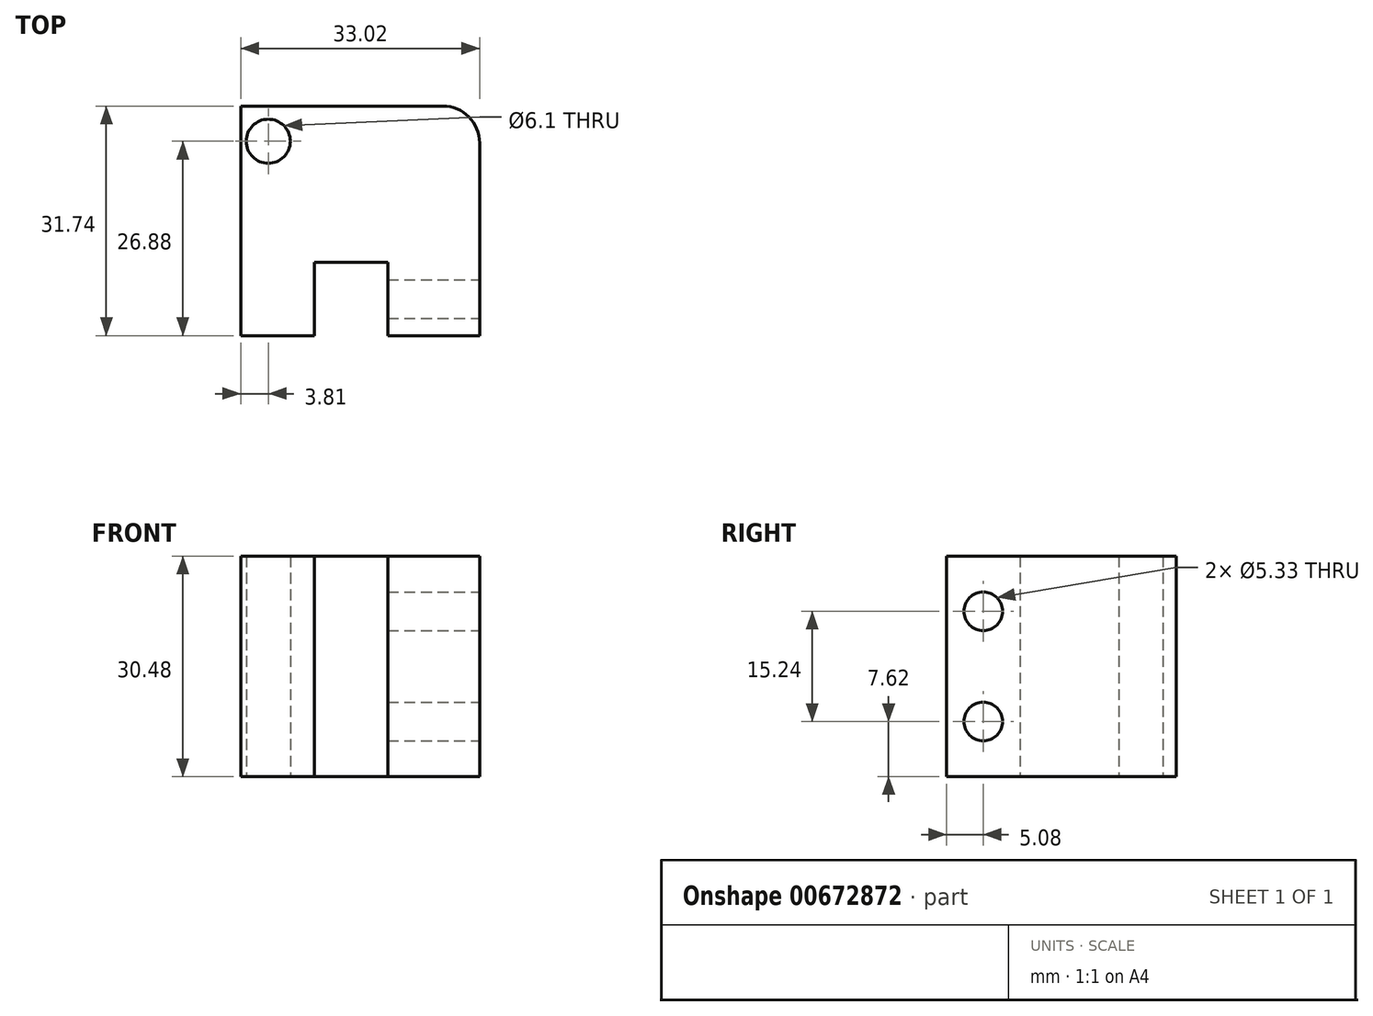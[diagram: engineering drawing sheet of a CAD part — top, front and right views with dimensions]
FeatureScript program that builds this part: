
annotation { "Feature Type Name" : "Feature", "Feature Type Description" : "" }
export const myFeature = defineFeature(function(context is Context, id is Id, definition is map)
    precondition{}
    {
        {
            var Q0;
            Q0=qCreatedBy(makeId("Top.planeOp"),FACE);
            var sketch = newSketch(context, id + "F0", { "sketchPlane" : qUnion([Q0])});
            skLineSegment(sketch, "E0.bottom", {"start": v(-10.16, -6.35) * mm, "end": v(0, -6.35) * mm});
            skLineSegment(sketch, "E0.right", {"start": v(12.7, -6.35) * mm, "end": v(12.7, 15.23) * mm});
            skPoint(sketch, "E0.middle", {"position": v(0, 0) * mm});
            skLineSegment(sketch, "E1", {"start": v(-10.16, -16.51) * mm, "end": v(-10.16, -6.35) * mm});
            skLineSegment(sketch, "E2", {"start": v(12.7, -6.35) * mm, "end": v(12.7, -16.51) * mm});
            skLineSegment(sketch, "E3", {"start": v(12.7, -16.51) * mm, "end": v(0, -16.51) * mm});
            skLineSegment(sketch, "E4", {"start": v(0, -16.51) * mm, "end": v(0, -6.35) * mm});
            skLineSegment(sketch, "E5", {"start": v(-10.16, -16.51) * mm, "end": v(-16.5, -16.51) * mm});
            skLineSegment(sketch, "E6", {"start": v(-17.15, 15.23) * mm, "end": v(12.7, 15.23) * mm});
            skLineSegment(sketch, "E7", {"start": v(-16.51, 8.95) * mm, "end": v(-16.5, -16.51) * mm});
            skLineSegment(sketch, "E8", {"start": v(-16.5, -16.51) * mm, "end": v(-20.32, -16.51) * mm});
            skLineSegment(sketch, "E9", {"start": v(-20.32, -16.51) * mm, "end": v(-20.32, 15.23) * mm});
            skLineSegment(sketch, "E10", {"start": v(-20.32, 15.23) * mm, "end": v(-17.15, 15.23) * mm});
            skLineSegment(sketch, "E11", {"start": v(-16.51, 8.95) * mm, "end": v(-16.51, 15.23) * mm, "construction": true});
            skCircle(sketch, "E12", {"center": v(-16.51, 10.37) * mm, "radius": 3.05 * mm});
            skSolve(sketch);
        }
        {
            var Q0;
            Q0=makeQuery(id+"F0.imprint","IMPRINT",FACE,{"disambiguationData":[TD([[makeQuery(id+"F0.imprint","IMPRINT",EDGE,{"derivedFrom":sQuery(id+"F0.wireOp",EDGE,"E0.bottom")}),1.0]])]});
            extrude(context, id + "F1", {"entities" : qUnion([Q0]), "depth" : 30.48 * mm, "offsetDistance" : 25.4 * mm});
        }
        {
            var Q0;
            Q0=makeQuery(id+"F1.opExtrude","SWEPT_FACE",FACE,{"disambiguationData":[OSD([sQuery(id+"F0.wireOp",EDGE,"E2")])]});
            var sketch = newSketch(context, id + "F2", { "sketchPlane" : qUnion([Q0])});
            skPoint(sketch, "E13.orphan", {"position": v(-16.51, 30.48) * mm});
            skPoint(sketch, "E14.end.orphan", {"position": v(15.23, 0) * mm});
            skLineSegment(sketch, "E15", {"start": v(-11.43, 30.48) * mm, "end": v(-11.43, 0) * mm, "construction": true});
            skLineSegment(sketch, "E16", {"start": v(-16.51, 7.62) * mm, "end": v(15.23, 7.62) * mm, "construction": true});
            skPoint(sketch, "E17.center.orphan", {"position": v(-11.43, 15.24) * mm});
            skCircle(sketch, "E18", {"center": v(-11.43, 7.62) * mm, "radius": 2.67 * mm});
            skLineSegment(sketch, "E19", {"start": v(-16.51, 22.86) * mm, "end": v(15.23, 22.86) * mm, "construction": true});
            skCircle(sketch, "E20", {"center": v(-11.43, 22.86) * mm, "radius": 2.67 * mm});
            skSolve(sketch);
        }
        {
            var Q0;
            Q0=makeQuery(id+"F2.imprint","IMPRINT",FACE,{"disambiguationData":[TD([[makeQuery(id+"F2.imprint","IMPRINT",EDGE,{"derivedFrom":sQuery(id+"F2.wireOp",EDGE,"E20")}),1.0]])]});
            var Q1;
            Q1=makeQuery(id+"F2.imprint","IMPRINT",FACE,{"disambiguationData":[TD([[makeQuery(id+"F2.imprint","IMPRINT",EDGE,{"derivedFrom":sQuery(id+"F2.wireOp",EDGE,"E18")}),1.0]])]});
            extrude(context, id + "F3", {"entities" : qUnion([Q0, Q1]), "operationType" : NewBodyOperationType.REMOVE, "endBound" : BoundingType.UP_TO_NEXT, "oppositeDirection" : true, "depth" : 25.4 * mm, "offsetDistance" : 25.4 * mm});
        }
        {
            var Q0;
            Q0=makeQuery(id+"F1.opExtrude","SWEPT_EDGE",EDGE,{"disambiguationData":[OSD([sQuery(id+"F0.wireOp",EDGE,"E0.right"),sQuery(id+"F0.wireOp",EDGE,"E6")])]});
            fillet(context, id + "F4", {"entities" : qUnion([Q0]), "radius" : 5.08 * mm, "tangentPropagation" : true, "allowEdgeOverflow" : false});
        }
    });
